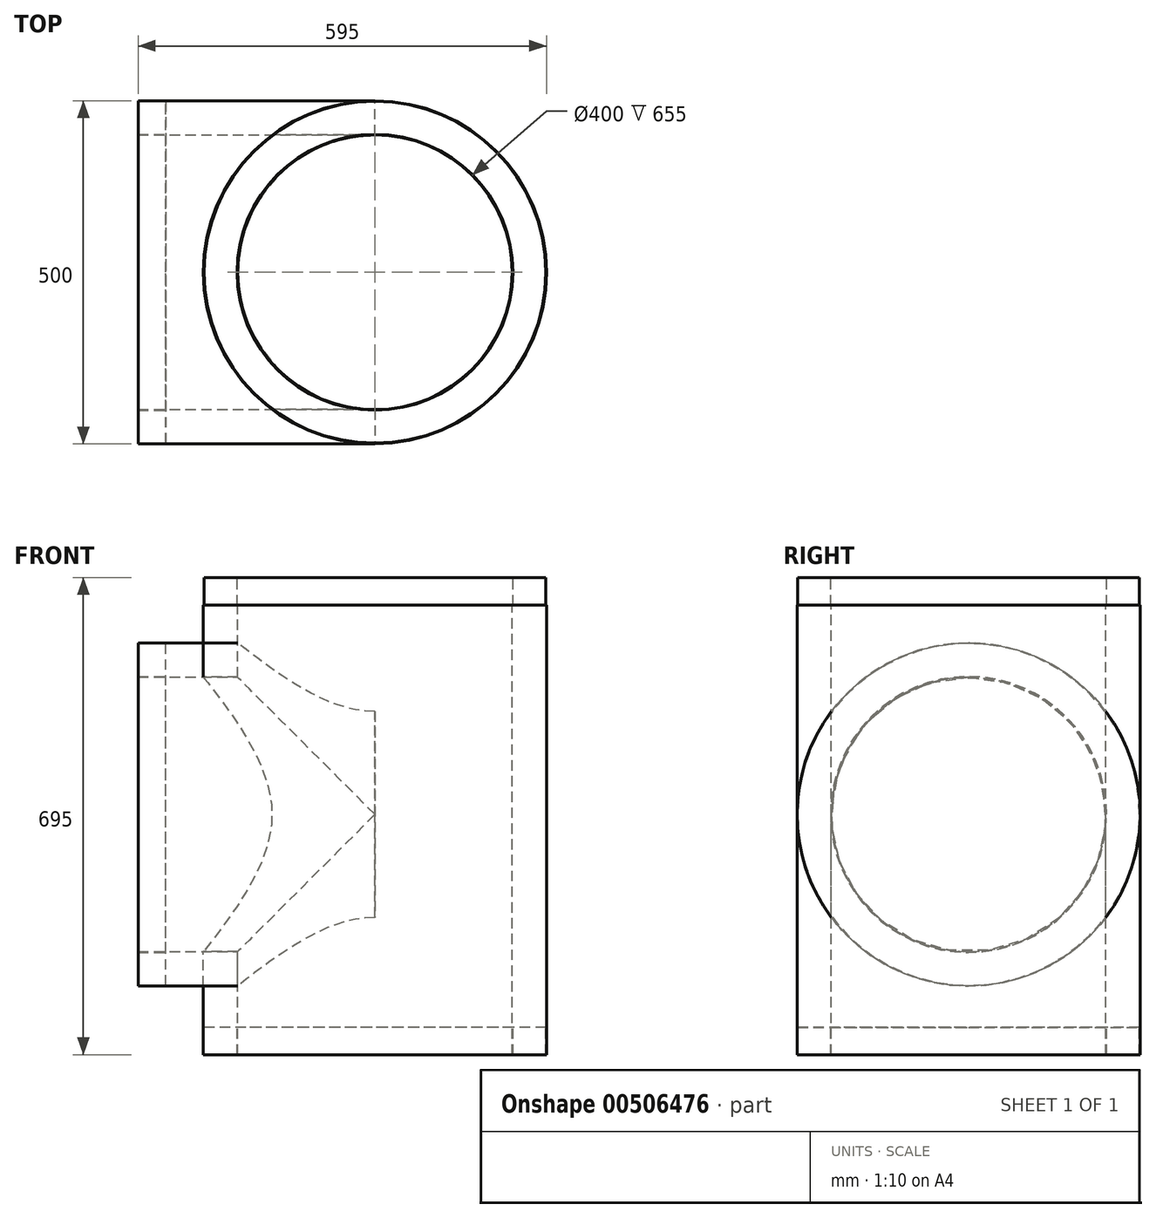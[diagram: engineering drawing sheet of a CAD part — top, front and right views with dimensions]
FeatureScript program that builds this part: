
annotation { "Feature Type Name" : "Feature", "Feature Type Description" : "" }
export const myFeature = defineFeature(function(context is Context, id is Id, definition is map)
    precondition{}
    {
        {
            var Q0;
            Q0=qCreatedBy(makeId("Front.planeOp"),FACE);
            var sketch = newSketch(context, id + "F0", { "sketchPlane" : qUnion([Q0])});
            skLineSegment(sketch, "E0", {"start": v(0, 722.18) * mm, "end": v(0, -793.11) * mm, "construction": true});
            skLineSegment(sketch, "E1", {"start": v(-200, -350) * mm, "end": v(-200, 305) * mm});
            skLineSegment(sketch, "E2", {"start": v(-200, 305) * mm, "end": v(-201, 305) * mm});
            skLineSegment(sketch, "E3", {"start": v(-201, 305) * mm, "end": v(-201, 345) * mm});
            skLineSegment(sketch, "E4", {"start": v(-201, 345) * mm, "end": v(-249, 345) * mm});
            skLineSegment(sketch, "E5", {"start": v(-249, 345) * mm, "end": v(-249, 305) * mm});
            skLineSegment(sketch, "E6", {"start": v(-249, 305) * mm, "end": v(-250, 305) * mm});
            skLineSegment(sketch, "E7", {"start": v(-250, 305) * mm, "end": v(-250, -350) * mm});
            skLineSegment(sketch, "E8", {"start": v(-250, -350) * mm, "end": v(-249, -350) * mm});
            skLineSegment(sketch, "E9", {"start": v(-249, -350) * mm, "end": v(-249, -310) * mm});
            skLineSegment(sketch, "E10", {"start": v(-249, -310) * mm, "end": v(-201, -310) * mm});
            skLineSegment(sketch, "E11", {"start": v(-201, -310) * mm, "end": v(-201, -350) * mm});
            skLineSegment(sketch, "E12", {"start": v(-201, -350) * mm, "end": v(-200, -350) * mm});
            skLineSegment(sketch, "E13", {"start": v(0, 0) * mm, "end": v(-528, 0) * mm, "construction": true});
            skLineSegment(sketch, "E14", {"start": v(0, -200) * mm, "end": v(-345, -200) * mm});
            skLineSegment(sketch, "E15", {"start": v(-345, -250) * mm, "end": v(0, -250) * mm});
            skLineSegment(sketch, "E16", {"start": v(0, -250) * mm, "end": v(0, -200) * mm});
            skLineSegment(sketch, "E17", {"start": v(-345, -200) * mm, "end": v(-345, -201) * mm});
            skLineSegment(sketch, "E18", {"start": v(-305, -201) * mm, "end": v(-345, -201) * mm});
            skLineSegment(sketch, "E19", {"start": v(-305, -201) * mm, "end": v(-305, -249) * mm});
            skLineSegment(sketch, "E20", {"start": v(-345, -249) * mm, "end": v(-305, -249) * mm});
            skLineSegment(sketch, "E21", {"start": v(-345, -249) * mm, "end": v(-345, -250) * mm});
            skSolve(sketch);
        }
        {
            var Q0;
            {var subQ0=sQuery(id+"F0.wireOp",EDGE,"E2");Q0=makeQuery(id+"F0.imprint","IMPRINT",FACE,{"disambiguationData":[TD([[makeQuery(id+"F0.imprint","IMPRINT",EDGE,{"derivedFrom":subQ0}),1.0]])]});}
            var Q1;
            {var subQ0=sQuery(id+"F0.wireOp",EDGE,"E15");var subQ1=sQuery(id+"F0.wireOp",EDGE,"E1");var subQ2=makeQuery(id+"F0.imprint","INTERSECT",VERTEX,{"derivedFrom":[subQ1,subQ0]});Q1=makeQuery(id+"F0.imprint","IMPRINT",FACE,{"disambiguationData":[TD([[makeQuery(id+"F0.imprint","IMPRINT",EDGE,{"disambiguationData":[TD([[subQ2,-1.0]])],"derivedFrom":subQ1}),1.0]])]});}
            var Q2;
            {var subQ0=sQuery(id+"F0.wireOp",EDGE,"E8");Q2=makeQuery(id+"F0.imprint","IMPRINT",FACE,{"disambiguationData":[TD([[makeQuery(id+"F0.imprint","IMPRINT",EDGE,{"derivedFrom":subQ0}),1.0]])]});}
            var Q3;
            Q3=sQuery(id+"F0.wireOp",EDGE,"E0");
            revolve(context, id + "F1", {"entities" : qUnion([Q0, Q1, Q2]), "axis" : qUnion([Q3]), "revolveType" : RevolveType.FULL});
        }
        {
            var Q0;
            {var subQ0=sQuery(id+"F0.wireOp",EDGE,"E17");Q0=makeQuery(id+"F0.imprint","IMPRINT",FACE,{"disambiguationData":[TD([[makeQuery(id+"F0.imprint","IMPRINT",EDGE,{"derivedFrom":subQ0}),1.0]])]});}
            var Q1;
            {var subQ5=sQuery(id+"F0.wireOp",EDGE,"E16");Q1=makeQuery(id+"F0.imprint","IMPRINT",FACE,{"disambiguationData":[TD([[makeQuery(id+"F0.imprint","IMPRINT",EDGE,{"derivedFrom":subQ5}),1.0]])]});}
            var Q2;
            {var subQ0=sQuery(id+"F0.wireOp",EDGE,"E15");var subQ1=sQuery(id+"F0.wireOp",EDGE,"E1");var subQ2=makeQuery(id+"F0.imprint","INTERSECT",VERTEX,{"derivedFrom":[subQ1,subQ0]});Q2=makeQuery(id+"F0.imprint","IMPRINT",FACE,{"disambiguationData":[TD([[makeQuery(id+"F0.imprint","IMPRINT",EDGE,{"disambiguationData":[TD([[subQ2,-1.0]])],"derivedFrom":subQ1}),1.0]])]});}
            var Q3;
            Q3=sQuery(id+"F0.wireOp",EDGE,"E13");
            revolve(context, id + "F2", {"surfaceOperationType" : NewSurfaceOperationType.NEW, "entities" : qUnion([Q0, Q1, Q2]), "axis" : qUnion([Q3]), "revolveType" : RevolveType.FULL});
        }
        {
            var Q0;
            Q0=makeQuery(id+"F2.opRevolve","SWEPT_FACE",FACE,{"disambiguationData":[OSD([sQuery(id+"F0.wireOp",EDGE,"E19")])]});
            var sketch = newSketch(context, id + "F3", { "sketchPlane" : qUnion([Q0])});
            skCircle(sketch, "E22.0", {"center": v(0, 0) * mm, "radius": 200 * mm});
            skSolve(sketch);
        }
        {
            var Q0;
            Q0 = qSketchRegion(id + "F3", true);
            var Q1;
            Q1=makeQuery(id+"F2.opRevolve","SWEPT_FACE",FACE,{"disambiguationData":[OSD([sQuery(id+"F0.wireOp",EDGE,"E16")])]});
            extrude(context, id + "F4", {"entities" : qUnion([Q0]), "operationType" : NewBodyOperationType.REMOVE, "endBound" : BoundingType.UP_TO_SURFACE, "oppositeDirection" : true, "depth" : 25 * mm, "endBoundEntityFace" : qUnion([Q1]), "offsetDistance" : 25 * mm});
        }
        {
            var Q0;
            Q0=makeQuery(id+"F1.opRevolve","SWEPT_FACE",FACE,{"disambiguationData":[OSD([sQuery(id+"F0.wireOp",EDGE,"E4")])]});
            var sketch = newSketch(context, id + "F5", { "sketchPlane" : qUnion([Q0])});
            skCircle(sketch, "E23", {"center": v(0, 0) * mm, "radius": 200 * mm});
            skSolve(sketch);
        }
        {
            var Q0;
            Q0=qSketchRegion(id+"F5",true);
            extrude(context, id + "F6", {"entities" : qUnion([Q0]), "operationType" : NewBodyOperationType.REMOVE, "oppositeDirection" : true, "depth" : 1200 * mm});
        }
    });
